# Revit family: 306_C215Q
name_source: partatom
category: Pipe Accessories
units: mm (PartAtom-declared; Revit-internal decimal feet)

## family parameters
Always vertical = Yes
Cut with Voids When Loaded = No
Part Type = Valve - Breaks Into
Round Connector Dimension = Use Diameter
Shared = No
Work Plane-Based = No

## types (1)
- C215Q
    CAT0 = Yes
    CenSd_R1_6 = 9 mm
    D = 15 mm
    Description = Zone valve, 2-way, Internal thread
    H1 = 3 mm  [stored 0.00984252 ft]
    HT = 12 mm  [stored 0.0393701 ft]
    L1 = 12 mm  [stored 0.0393701 ft]
    L11 = 29 mm  [stored 0.0951444 ft]
    L12 = 17 mm
    L13 = 15 mm  [stored 0.0492126 ft]
    L1__ve = -12 mm  [stored -0.0393701 ft]
    L2D = 58 mm
    L2D_Min = 3048 mm  [stored 10 ft]
    L3 = 31 mm
    MC_Default_elevation = 0 mm  [stored 0 ft]
    Manufacturer = Belimo
    QmdConnectorList = 301;D;302;D
    R1 = 11 mm
    R2 = 10 mm  [stored 0.0328084 ft]
    W2D = 15 mm  [stored 0.0492126 ft]
    magiPartTypeId = 306
    magiProductCode = C215Q
    magiProductFamilyId = C215Q
    magiProductId = C215Q

note: [stored X ft] marks values corroborated as IEEE doubles in the binary element streams (Revit-internal decimal feet)

## geometry (parser evidence)
native form markers: Sweep x2
no freeform markers — native parametric forms only
